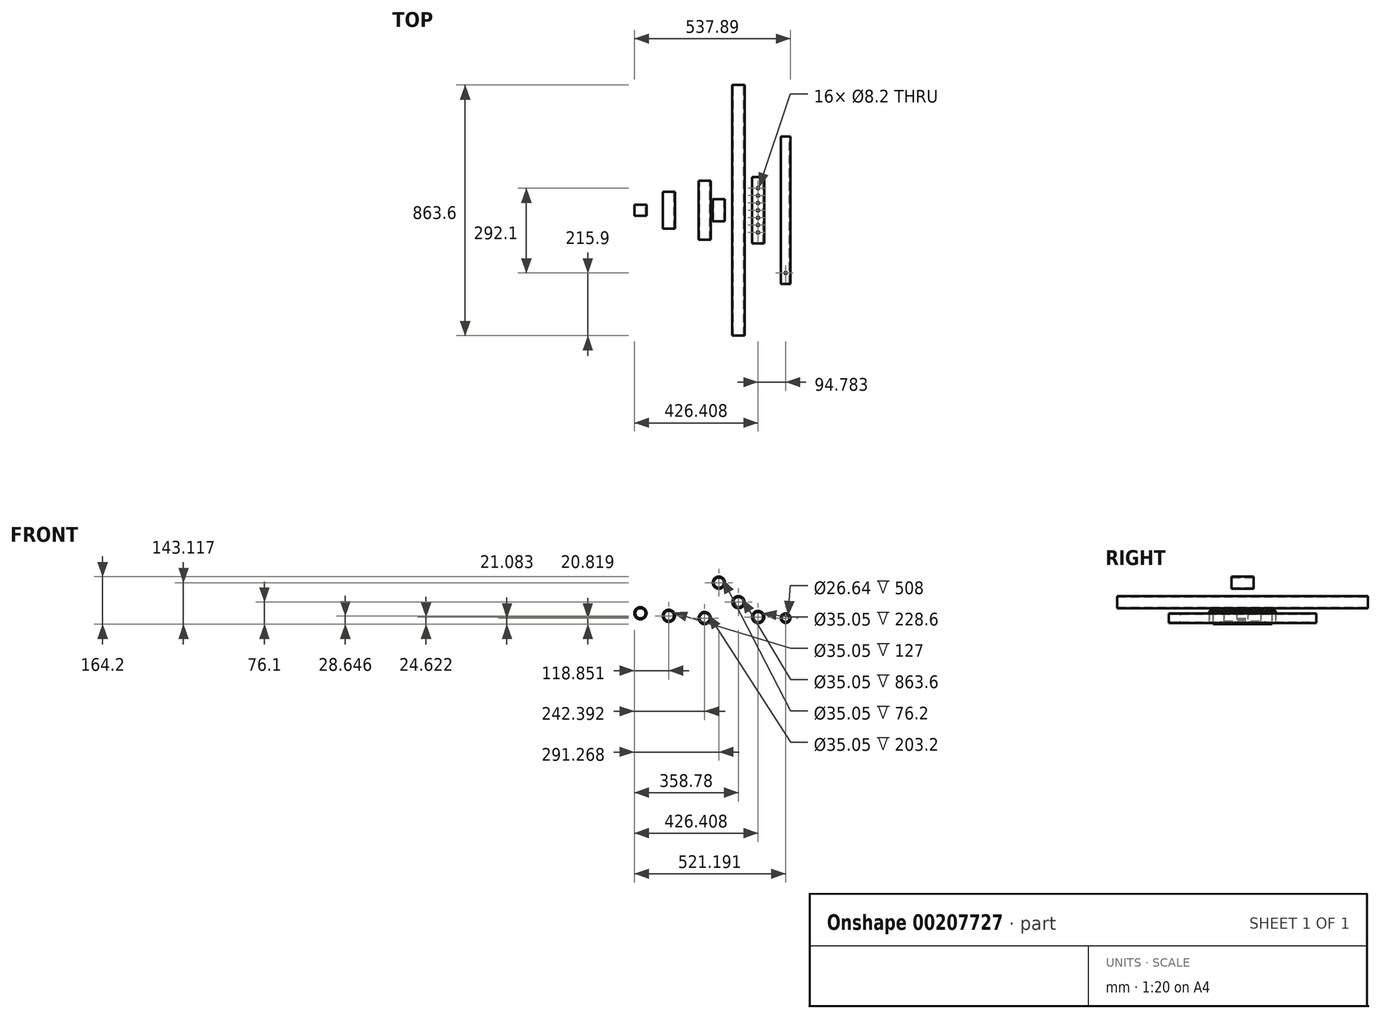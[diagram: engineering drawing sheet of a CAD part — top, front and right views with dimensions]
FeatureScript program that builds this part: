
annotation { "Feature Type Name" : "Feature", "Feature Type Description" : "" }
export const myFeature = defineFeature(function(context is Context, id is Id, definition is map)
    precondition{}
    {
        {
            var Q0;
            Q0=qCreatedBy(makeId("Front.planeOp"),FACE);
            var sketch = newSketch(context, id + "F0", { "sketchPlane" : qUnion([Q0])});
            skCircle(sketch, "E0", {"center": v(0, 0) * mm, "radius": 21.08 * mm});
            skCircle(sketch, "E1", {"center": v(0, 0) * mm, "radius": 17.53 * mm});
            skSolve(sketch);
        }
        {
            var Q0;
            Q0 = qSketchRegion(id + "F0", true);
            extrude(context, id + "F1", {"entities" : qUnion([Q0]), "endBound" : BoundingType.SYMMETRIC, "depth" : 863.6 * mm});
        }
        {
            var Q0;
            Q0=qCreatedBy(makeId("Front.planeOp"),FACE);
            var sketch = newSketch(context, id + "F2", { "sketchPlane" : qUnion([Q0])});
            skCircle(sketch, "E2", {"center": v(67.63, -51.48) * mm, "radius": 21.08 * mm});
            skCircle(sketch, "E3", {"center": v(67.63, -51.48) * mm, "radius": 17.53 * mm});
            skSolve(sketch);
        }
        {
            var Q0;
            Q0=makeQuery(id+"F2.imprint","IMPRINT",FACE,{"disambiguationData":[TD([[makeQuery(id+"F2.imprint","IMPRINT",EDGE,{"derivedFrom":sQuery(id+"F2.wireOp",EDGE,"E2")}),1.0]])]});
            extrude(context, id + "F3", {"entities" : qUnion([Q0]), "endBound" : BoundingType.SYMMETRIC, "depth" : 228.6 * mm});
        }
        {
            var Q0;
            Q0=qCreatedBy(makeId("Front.planeOp"),FACE);
            var sketch = newSketch(context, id + "F4", { "sketchPlane" : qUnion([Q0])});
            skCircle(sketch, "E4", {"center": v(162.41, -55.28) * mm, "radius": 16.7 * mm});
            skCircle(sketch, "E5", {"center": v(162.41, -55.28) * mm, "radius": 13.32 * mm});
            skSolve(sketch);
        }
        {
            var Q0;
            Q0 = qSketchRegion(id + "F4", true);
            extrude(context, id + "F5", {"entities" : qUnion([Q0]), "endBound" : BoundingType.SYMMETRIC, "depth" : 508 * mm});
        }
        {
            var Q0;
            Q0=qCreatedBy(makeId("Front.planeOp"),FACE);
            var sketch = newSketch(context, id + "F6", { "sketchPlane" : qUnion([Q0])});
            skCircle(sketch, "E6", {"center": v(249, -55.4) * mm, "radius": 16.7 * mm});
            skCircle(sketch, "E7", {"center": v(249, -55.4) * mm, "radius": 13.32 * mm});
            skSolve(sketch);
        }
        {
            var Q0;
            Q0=makeQuery(id+"F6.imprint","IMPRINT",FACE,{"disambiguationData":[TD([[makeQuery(id+"F6.imprint","IMPRINT",EDGE,{"derivedFrom":sQuery(id+"F6.wireOp",EDGE,"E6")}),1.0]])]});
            var Q1;
            Q1=sQuery(id+"F6.wireOp",EDGE,"E6");
            var Q2;
            Q2=sQuery(id+"F6.wireOp",EDGE,"E7");
            extrude(context, id + "F7", {"entities" : qUnion([Q0]), "surfaceEntities" : qUnion([Q1, Q2]), "endBound" : BoundingType.SYMMETRIC, "depth" : 873.12 * mm});
        }
        {
            var Q0;
            Q0=qCreatedBy(makeId("Front.planeOp"),FACE);
            var sketch = newSketch(context, id + "F8", { "sketchPlane" : qUnion([Q0])});
            skCircle(sketch, "E8", {"center": v(-67.51, 67.02) * mm, "radius": 21.08 * mm});
            skCircle(sketch, "E9", {"center": v(-67.51, 67.02) * mm, "radius": 17.53 * mm});
            skSolve(sketch);
        }
        {
            var Q0;
            Q0=makeQuery(id+"F8.imprint","IMPRINT",FACE,{"disambiguationData":[TD([[makeQuery(id+"F8.imprint","IMPRINT",EDGE,{"derivedFrom":sQuery(id+"F8.wireOp",EDGE,"E8")}),1.0]])]});
            var Q1;
            Q1=sQuery(id+"F8.wireOp",EDGE,"E8");
            var Q2;
            Q2=sQuery(id+"F8.wireOp",EDGE,"E9");
            extrude(context, id + "F9", {"entities" : qUnion([Q0]), "surfaceEntities" : qUnion([Q1, Q2]), "endBound" : BoundingType.SYMMETRIC, "depth" : 76.2 * mm});
        }
        {
            var Q0;
            Q0=qCreatedBy(makeId("Top.planeOp"),FACE);
            var sketch = newSketch(context, id + "F10", { "sketchPlane" : qUnion([Q0])});
            skPoint(sketch, "E10", {"position": v(67.63, 76.2) * mm});
            skPoint(sketch, "E11", {"position": v(162.41, -215.9) * mm});
            skLineSegment(sketch, "E12", {"start": v(88.7, 114.3) * mm, "end": v(88.7, -101.6) * mm});
            skLineSegment(sketch, "E13", {"start": v(46.55, -101.6) * mm, "end": v(46.55, 114.3) * mm});
            skLineSegment(sketch, "E14", {"start": v(179.11, 254) * mm, "end": v(179.11, -158.75) * mm});
            skLineSegment(sketch, "E15", {"start": v(145.71, -158.75) * mm, "end": v(145.71, 254) * mm});
            skLineSegment(sketch, "E16", {"start": v(46.55, 114.3) * mm, "end": v(88.7, 114.3) * mm});
            skLineSegment(sketch, "E17", {"start": v(145.71, 254) * mm, "end": v(179.11, 254) * mm});
            skLineSegment(sketch, "E18", {"start": v(67.63, 114.3) * mm, "end": v(67.63, 76.2) * mm, "construction": true});
            skLineSegment(sketch, "E19", {"start": v(162.41, -215.9) * mm, "end": v(162.41, 254) * mm, "construction": true});
            skPoint(sketch, "E20.0.1.0", {"position": v(67.63, 50.8) * mm});
            skPoint(sketch, "E20.0.2.0", {"position": v(67.63, 25.4) * mm});
            skLineSegment(sketch, "E20.direction1", {"start": v(67.63, 76.2) * mm, "end": v(126.27, 76.2) * mm, "construction": true});
            skLineSegment(sketch, "E20.direction2", {"start": v(67.63, 76.2) * mm, "end": v(67.63, 50.8) * mm, "construction": true});
            skPoint(sketch, "E21.0.0.3", {"position": v(67.63, 0) * mm});
            skPoint(sketch, "E21.0.0.4", {"position": v(67.63, -25.4) * mm});
            skPoint(sketch, "E21.0.0.5", {"position": v(67.63, -50.8) * mm});
            skPoint(sketch, "E21.0.0.6", {"position": v(67.63, -76.2) * mm});
            skSolve(sketch);
        }
        {
            var Q0;
            Q0=sQuery(id+"F10.wireOp",VERTEX,"E10");
            var Q1;
            Q1=sQuery(id+"F10.wireOp",VERTEX,"E20.0.1.0");
            var Q2;
            Q2=sQuery(id+"F10.wireOp",VERTEX,"E20.0.2.0");
            var Q3;
            Q3=sQuery(id+"F10.wireOp",VERTEX,"E20.0.3.0");
            var Q4;
            Q4=sQuery(id+"F10.wireOp",VERTEX,"E20.0.4.0");
            var Q5;
            Q5=sQuery(id+"F10.wireOp",VERTEX,"E20.0.5.0");
            var Q6;
            Q6=sQuery(id+"F10.wireOp",VERTEX,"E11");
            var Q7;
            Q7=sQuery(id+"F10.wireOp",VERTEX,"2916ee7a-e89e-41ec-a014-c4c362c6726b.0.0.6");
            var Q8;
            Q8=sQuery(id+"F10.wireOp",VERTEX,"2916ee7a-e89e-41ec-a014-c4c362c6726b.0.0.7");
            var Q9;
            Q9=sQuery(id+"F10.wireOp",VERTEX,"E21.0.0.3");
            var Q10;
            Q10=sQuery(id+"F10.wireOp",VERTEX,"E21.0.0.4");
            var Q11;
            Q11=sQuery(id+"F10.wireOp",VERTEX,"E21.0.0.5");
            var Q12;
            Q12=sQuery(id+"F10.wireOp",VERTEX,"E21.0.0.6");
            var Q13;
            Q13=sQuery(id+"F10.wireOp",VERTEX,"E21.0.0.7");
            var Q14;
            Q14=makeQuery(id+"F3.opExtrude","SWEPT_BODY",BODY,{"disambiguationData":[OSD([sQuery(id+"F2.wireOp",EDGE,"E2"),sQuery(id+"F2.wireOp",EDGE,"E3")])]});
            var Q15;
            Q15=makeQuery(id+"F5.opExtrude","SWEPT_BODY",BODY,{"disambiguationData":[OSD([sQuery(id+"F4.wireOp",EDGE,"E4"),sQuery(id+"F4.wireOp",EDGE,"E5")])]});
            hole(context, id + "F11", {"style" : HoleStyle.SIMPLE, "endStyle" : HoleEndStyle.THROUGH, "standardTappedOrClearance" : lookupTablePath({ "standard" : "ISO", "size" : "8.2", "type" : "Drilled" }), "standardBlindInLast" : lookupTablePath({ "standard" : "ISO", "size" : "8.2", "type" : "Drilled" }), "holeDiameter" : 8.2 * mm, "startFromSketch" : true, "locations" : qUnion([Q0, Q1, Q2, Q3, Q4, Q5, Q6, Q7, Q8, Q9, Q10, Q11, Q12, Q13]), "scope" : qUnion([Q14, Q15]), "tappedDepth" : 12.7 * mm, "tapClearance" : 3});
        }
        {
            var Q0;
            Q0=qCreatedBy(makeId("Front.planeOp"),FACE);
            var sketch = newSketch(context, id + "F12", { "sketchPlane" : qUnion([Q0])});
            skCircle(sketch, "E22", {"center": v(-116.39, -55.02) * mm, "radius": 21.08 * mm});
            skCircle(sketch, "E23", {"center": v(-116.39, -55.02) * mm, "radius": 17.53 * mm});
            skSolve(sketch);
        }
        {
            var Q0;
            Q0=makeQuery(id+"F12.imprint","IMPRINT",FACE,{"disambiguationData":[TD([[makeQuery(id+"F12.imprint","IMPRINT",EDGE,{"derivedFrom":sQuery(id+"F12.wireOp",EDGE,"E22")}),1.0]])]});
            var Q1;
            Q1=sQuery(id+"F12.wireOp",EDGE,"E22");
            var Q2;
            Q2=sQuery(id+"F12.wireOp",EDGE,"E23");
            extrude(context, id + "F13", {"entities" : qUnion([Q0]), "surfaceEntities" : qUnion([Q1, Q2]), "endBound" : BoundingType.SYMMETRIC, "depth" : 203.2 * mm});
        }
        {
            var Q0;
            Q0=qCreatedBy(makeId("Front.planeOp"),FACE);
            var sketch = newSketch(context, id + "F14", { "sketchPlane" : qUnion([Q0])});
            skCircle(sketch, "E24", {"center": v(-239.93, -47.45) * mm, "radius": 21.08 * mm});
            skCircle(sketch, "E25", {"center": v(-239.93, -47.45) * mm, "radius": 17.53 * mm});
            skSolve(sketch);
        }
        {
            var Q0;
            Q0=makeQuery(id+"F14.imprint","IMPRINT",FACE,{"disambiguationData":[TD([[makeQuery(id+"F14.imprint","IMPRINT",EDGE,{"derivedFrom":sQuery(id+"F14.wireOp",EDGE,"E24")}),1.0]])]});
            var Q1;
            Q1=sQuery(id+"F14.wireOp",EDGE,"E24");
            var Q2;
            Q2=sQuery(id+"F14.wireOp",EDGE,"E25");
            extrude(context, id + "F15", {"entities" : qUnion([Q0]), "surfaceEntities" : qUnion([Q1, Q2]), "endBound" : BoundingType.SYMMETRIC, "depth" : 127 * mm});
        }
        {
            var Q0;
            Q0=qCreatedBy(makeId("Front.planeOp"),FACE);
            var sketch = newSketch(context, id + "F16", { "sketchPlane" : qUnion([Q0])});
            skCircle(sketch, "E26", {"center": v(-337.7, -38.37) * mm, "radius": 21.08 * mm});
            skCircle(sketch, "E27", {"center": v(-337.7, -38.37) * mm, "radius": 17.53 * mm});
            skSolve(sketch);
        }
        {
            var Q0;
            Q0=makeQuery(id+"F16.imprint","IMPRINT",FACE,{"disambiguationData":[TD([[makeQuery(id+"F16.imprint","IMPRINT",EDGE,{"derivedFrom":sQuery(id+"F16.wireOp",EDGE,"E26")}),1.0]])]});
            var Q1;
            Q1=sQuery(id+"F16.wireOp",EDGE,"E26");
            var Q2;
            Q2=sQuery(id+"F16.wireOp",EDGE,"E27");
            extrude(context, id + "F17", {"entities" : qUnion([Q0]), "surfaceEntities" : qUnion([Q1, Q2]), "endBound" : BoundingType.SYMMETRIC, "depth" : 38.1 * mm});
        }
        {
            var Q0;
            Q0=makeQuery(id+"F7.opExtrude","SWEPT_BODY",BODY,{"disambiguationData":[OSD([sQuery(id+"F6.wireOp",EDGE,"E6"),sQuery(id+"F6.wireOp",EDGE,"E7")])]});
            deleteBodies(context, id + "F18", {"entities" : qUnion([Q0])});
        }
    });
